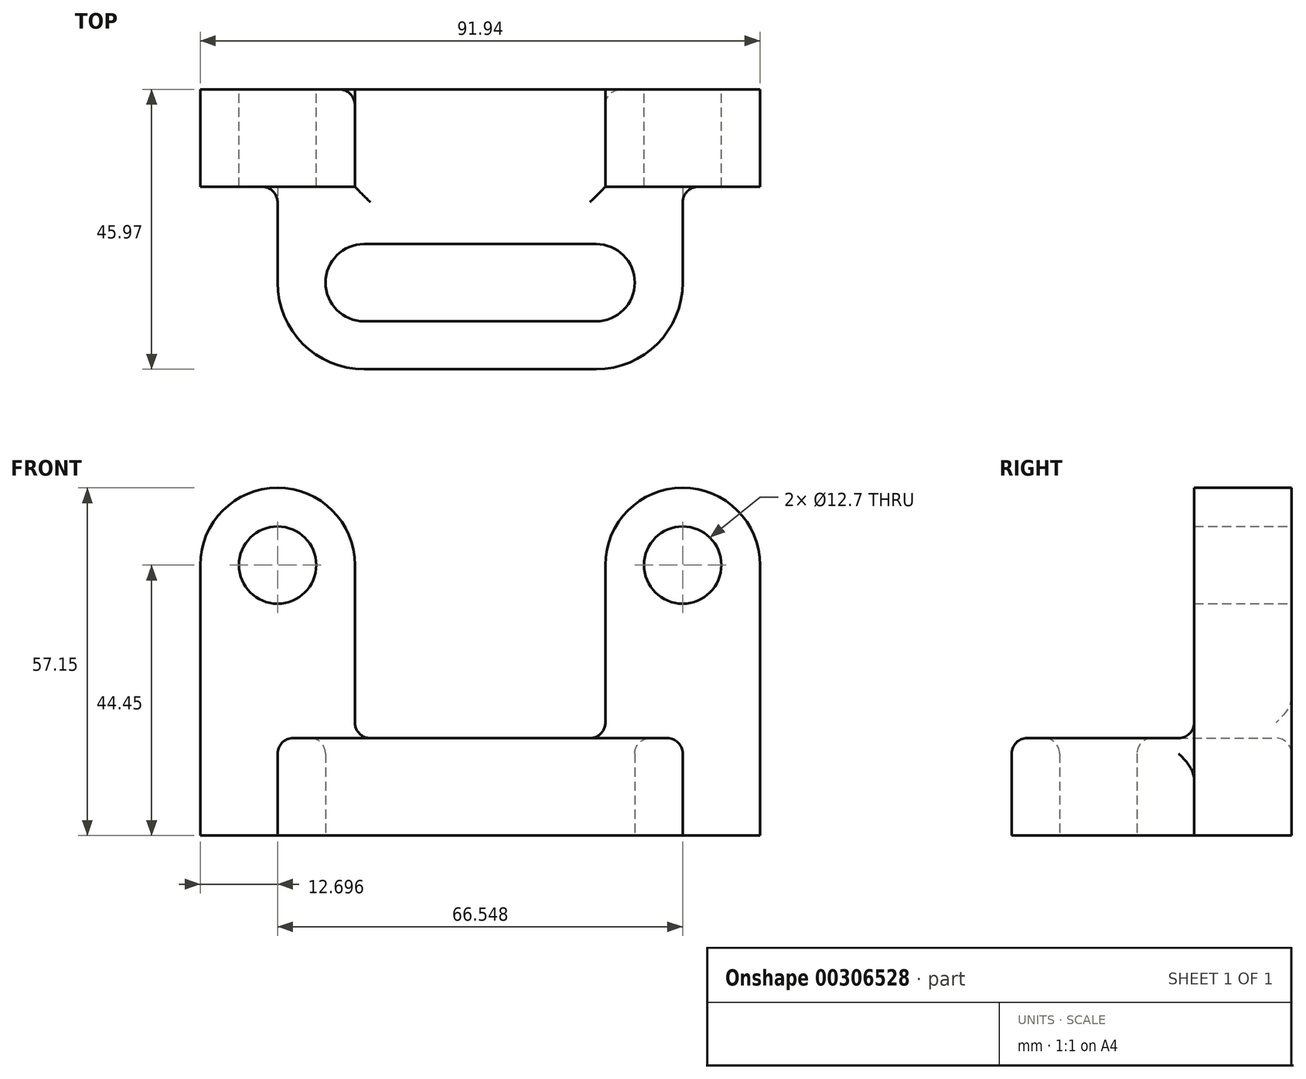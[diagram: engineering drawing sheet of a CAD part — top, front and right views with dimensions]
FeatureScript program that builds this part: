
annotation { "Feature Type Name" : "Feature", "Feature Type Description" : "" }
export const myFeature = defineFeature(function(context is Context, id is Id, definition is map)
    precondition{}
    {
        {
            var Q0;
            Q0=qCreatedBy(makeId("Top.planeOp"),FACE);
            var sketch = newSketch(context, id + "F0", { "sketchPlane" : qUnion([Q0])});
            skLineSegment(sketch, "E0.bottom", {"start": v(0, 0) * mm, "end": v(38.1, 0) * mm});
            skLineSegment(sketch, "E0.top", {"start": v(0, 12.7) * mm, "end": v(38.1, 12.7) * mm});
            skArc(sketch, "E1", {"start": v(0, 12.7) * mm, "mid": v(-6.35, 6.35) * mm, "end": v(0, 0) * mm});
            skArc(sketch, "E2", {"start": v(38.1, 0) * mm, "mid": v(44.45, 6.35) * mm, "end": v(38.1, 12.7) * mm});
            skArc(sketch, "E3", {"start": v(52.32, 6.35) * mm, "mid": v(48.16, -3.7) * mm, "end": v(38.1, -7.87) * mm});
            skPoint(sketch, "E4.startSnap0", {"position": v(-6.35, 6.35) * mm});
            skArc(sketch, "E5", {"start": v(-14.22, 6.35) * mm, "mid": v(-10.06, -3.7) * mm, "end": v(0, -7.87) * mm});
            skLineSegment(sketch, "E6", {"start": v(0, -7.87) * mm, "end": v(38.1, -7.87) * mm});
            skPoint(sketch, "E7.positionSnap0", {"position": v(19.05, 12.7) * mm});
            skLineSegment(sketch, "E8", {"start": v(-14.22, 6.35) * mm, "end": v(-14.22, 38.1) * mm});
            skLineSegment(sketch, "E9", {"start": v(52.32, 6.35) * mm, "end": v(52.32, 38.1) * mm});
            skLineSegment(sketch, "E10", {"start": v(-14.22, 38.1) * mm, "end": v(52.32, 38.1) * mm});
            skSolve(sketch);
        }
        {
            var Q0;
            Q0=makeQuery(id+"F0.imprint","IMPRINT",FACE,{"disambiguationData":[TD([[makeQuery(id+"F0.imprint","IMPRINT",EDGE,{"derivedFrom":sQuery(id+"F0.wireOp",EDGE,"E0.bottom")}),-1.0]])]});
            extrude(context, id + "F1", {"entities" : qUnion([Q0]), "depth" : 16 * mm});
        }
        {
            var Q0;
            Q0=makeQuery(id+"F1.opExtrude","SWEPT_FACE",FACE,{"disambiguationData":[OSD([sQuery(id+"F0.wireOp",EDGE,"E10")])]});
            var sketch = newSketch(context, id + "F2", { "sketchPlane" : qUnion([Q0])});
            skPoint(sketch, "E11", {"position": v(-52.32, 16) * mm});
            skPoint(sketch, "E12", {"position": v(14.22, 16) * mm});
            skLineSegment(sketch, "E13.bottom", {"start": v(26.92, 44.45) * mm, "end": v(20.57, 44.45) * mm});
            skLineSegment(sketch, "E13.left", {"start": v(26.92, 44.45) * mm, "end": v(26.92, 0) * mm});
            skLineSegment(sketch, "E13.right", {"start": v(1.52, 44.45) * mm, "end": v(1.52, 0) * mm});
            skPoint(sketch, "E13.middle", {"position": v(14.22, 0) * mm});
            skLineSegment(sketch, "E14", {"start": v(1.52, 0) * mm, "end": v(26.92, 0) * mm});
            skPoint(sketch, "E13.top.end.orphan", {"position": v(1.52, -44.45) * mm});
            skPoint(sketch, "E13.top.start.orphan", {"position": v(26.92, -44.45) * mm});
            skCircle(sketch, "E15", {"center": v(14.22, 44.45) * mm, "radius": 6.35 * mm});
            skArc(sketch, "E16", {"start": v(26.92, 44.45) * mm, "mid": v(14.22, 57.15) * mm, "end": v(1.52, 44.45) * mm});
            skLineSegment(sketch, "E17.trimOffspring", {"start": v(7.87, 44.45) * mm, "end": v(1.52, 44.45) * mm});
            skLineSegment(sketch, "E18.bottom", {"start": v(-39.62, 44.45) * mm, "end": v(-45.97, 44.45) * mm});
            skLineSegment(sketch, "E18.left", {"start": v(-39.62, 44.45) * mm, "end": v(-39.62, 0) * mm});
            skLineSegment(sketch, "E18.right", {"start": v(-65.02, 44.45) * mm, "end": v(-65.02, 0) * mm});
            skPoint(sketch, "E18.middle", {"position": v(-52.32, 0) * mm});
            skLineSegment(sketch, "E19", {"start": v(-65.02, 0) * mm, "end": v(-39.62, 0) * mm});
            skPoint(sketch, "E18.top.end.orphan", {"position": v(-65.02, -44.45) * mm});
            skPoint(sketch, "E18.top.start.orphan", {"position": v(-39.62, -44.45) * mm});
            skCircle(sketch, "E20", {"center": v(-52.32, 44.45) * mm, "radius": 6.35 * mm});
            skArc(sketch, "E21", {"start": v(-39.62, 44.45) * mm, "mid": v(-52.32, 57.15) * mm, "end": v(-65.02, 44.45) * mm});
            skLineSegment(sketch, "E22.trimOffspring", {"start": v(-58.67, 44.45) * mm, "end": v(-65.02, 44.45) * mm});
            skSolve(sketch);
        }
        {
            var Q0;
            Q0 = qSketchRegion(id + "F2", true);
            extrude(context, id + "F3", {"entities" : qUnion([Q0]), "operationType" : NewBodyOperationType.ADD, "oppositeDirection" : true, "depth" : 16 * mm});
        }
        {
            var Q0;
            Q0=makeQuery(id+"F1.opExtrude","CAP_EDGE",EDGE,{"disambiguationData":[OSD([sQuery(id+"F0.wireOp",EDGE,"E9")])],"isStart":false});
            var Q1;
            Q1=makeQuery(id+"F1.opExtrude","CAP_FACE",FACE,{"disambiguationData":[OSD([sQuery(id+"F0.wireOp",EDGE,"E0.bottom"),sQuery(id+"F0.wireOp",EDGE,"E0.top"),sQuery(id+"F0.wireOp",EDGE,"E1"),sQuery(id+"F0.wireOp",EDGE,"E2"),sQuery(id+"F0.wireOp",EDGE,"E3"),sQuery(id+"F0.wireOp",EDGE,"E5"),sQuery(id+"F0.wireOp",EDGE,"E6"),sQuery(id+"F0.wireOp",EDGE,"E8"),sQuery(id+"F0.wireOp",EDGE,"E9"),sQuery(id+"F0.wireOp",EDGE,"E10")])],"isStart":false});
            fillet(context, id + "F4", {"entities" : qUnion([Q0, Q1]), "radius" : 2.54 * mm, "tangentPropagation" : true, "allowEdgeOverflow" : false});
        }
    });
